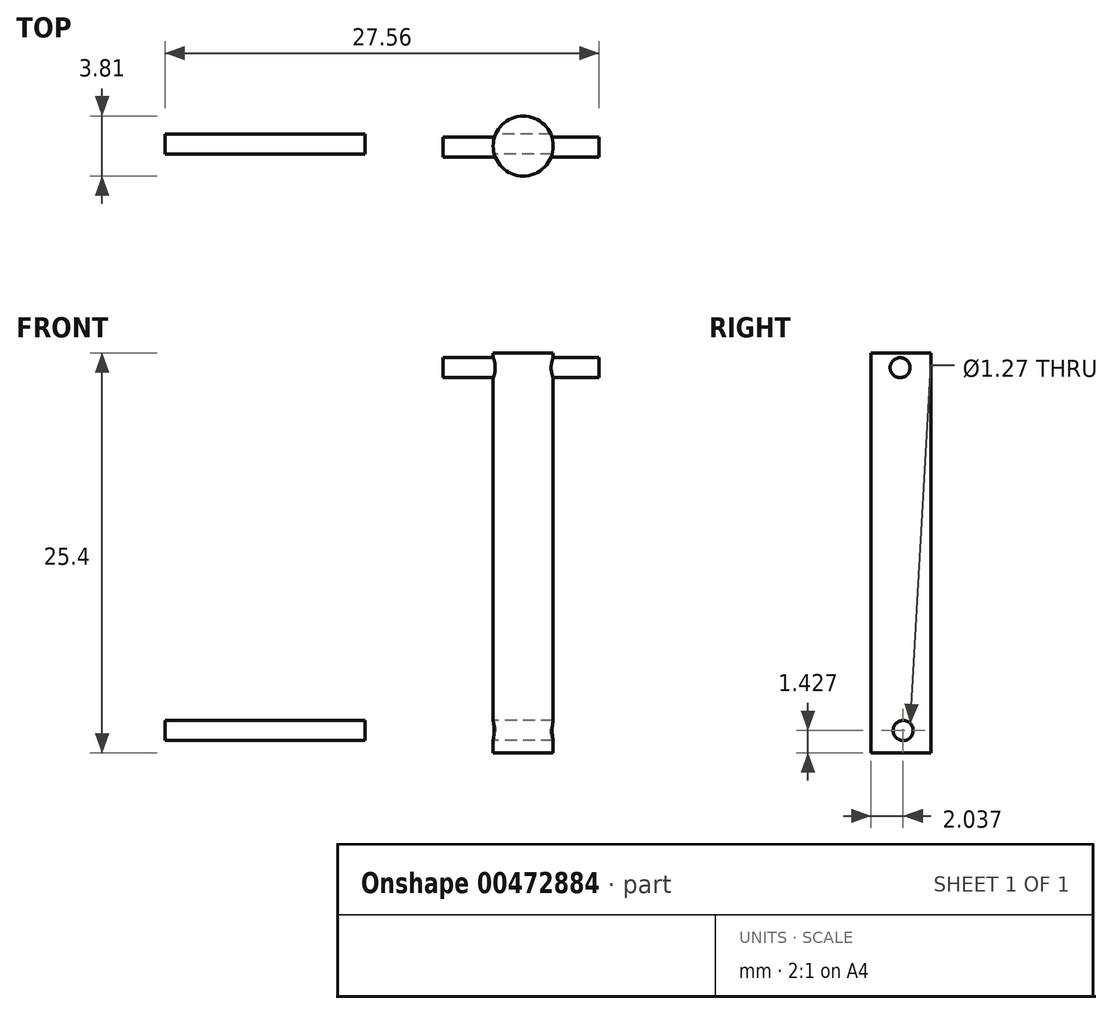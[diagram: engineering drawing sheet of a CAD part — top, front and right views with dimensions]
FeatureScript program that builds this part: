
annotation { "Feature Type Name" : "Feature", "Feature Type Description" : "" }
export const myFeature = defineFeature(function(context is Context, id is Id, definition is map)
    precondition{}
    {
        {
            var Q0;
            Q0=qCreatedBy(makeId("Top.planeOp"),FACE);
            var sketch = newSketch(context, id + "F0", { "sketchPlane" : qUnion([Q0])});
            skCircle(sketch, "E0", {"center": v(22.74, 23.96) * mm, "radius": 1.9 * mm});
            skSolve(sketch);
        }
        {
            var Q0;
            Q0=makeQuery(id+"F0.imprint","IMPRINT",FACE,{"disambiguationData":[TD([[makeQuery(id+"F0.imprint","IMPRINT",EDGE,{"derivedFrom":sQuery(id+"F0.wireOp",EDGE,"E0")}),1.0]])]});
            extrude(context, id + "F1", {"entities" : qUnion([Q0]), "depth" : 25.4 * mm});
        }
        {
            var Q0;
            Q0=qCreatedBy(makeId("Right.planeOp"),FACE);
            var sketch = newSketch(context, id + "F2", { "sketchPlane" : qUnion([Q0])});
            skCircle(sketch, "E1", {"center": v(23.9, 24.47) * mm, "radius": 0.64 * mm});
            skSolve(sketch);
        }
        {
            var Q0;
            Q0=makeQuery(id+"F2.imprint","IMPRINT",FACE,{"disambiguationData":[TD([[makeQuery(id+"F2.imprint","IMPRINT",EDGE,{"derivedFrom":sQuery(id+"F2.wireOp",EDGE,"E1")}),1.0]])]});
            extrude(context, id + "F3", {"entities" : qUnion([Q0]), "operationType" : NewBodyOperationType.ADD, "depth" : 27.56 * mm});
        }
        {
            var Q0;
            Q0=makeQuery(id+"F3.opExtrude","CAP_FACE",FACE,{"disambiguationData":[OSD([sQuery(id+"F2.wireOp",EDGE,"E1")])],"isStart":true});
            extrude(context, id + "F4", {"entities" : qUnion([Q0]), "operationType" : NewBodyOperationType.REMOVE, "oppositeDirection" : true, "depth" : 17.65 * mm});
        }
        {
            var Q0;
            Q0=qCreatedBy(makeId("Right.planeOp"),FACE);
            var sketch = newSketch(context, id + "F5", { "sketchPlane" : qUnion([Q0])});
            skCircle(sketch, "E2", {"center": v(24.1, 1.43) * mm, "radius": 0.64 * mm});
            skSolve(sketch);
        }
        {
            var Q0;
            Q0=makeQuery(id+"F5.imprint","IMPRINT",FACE,{"disambiguationData":[TD([[makeQuery(id+"F5.imprint","IMPRINT",EDGE,{"derivedFrom":sQuery(id+"F5.wireOp",EDGE,"E2")}),1.0]])]});
            extrude(context, id + "F6", {"entities" : qUnion([Q0]), "operationType" : NewBodyOperationType.REMOVE, "depth" : 46.23 * mm});
        }
        {
            var Q0;
            Q0=makeQuery(id+"F5.imprint","IMPRINT",FACE,{"disambiguationData":[TD([[makeQuery(id+"F5.imprint","IMPRINT",EDGE,{"derivedFrom":sQuery(id+"F5.wireOp",EDGE,"E2")}),1.0]])]});
            extrude(context, id + "F7", {"entities" : qUnion([Q0]), "depth" : 12.7 * mm});
        }
    });
